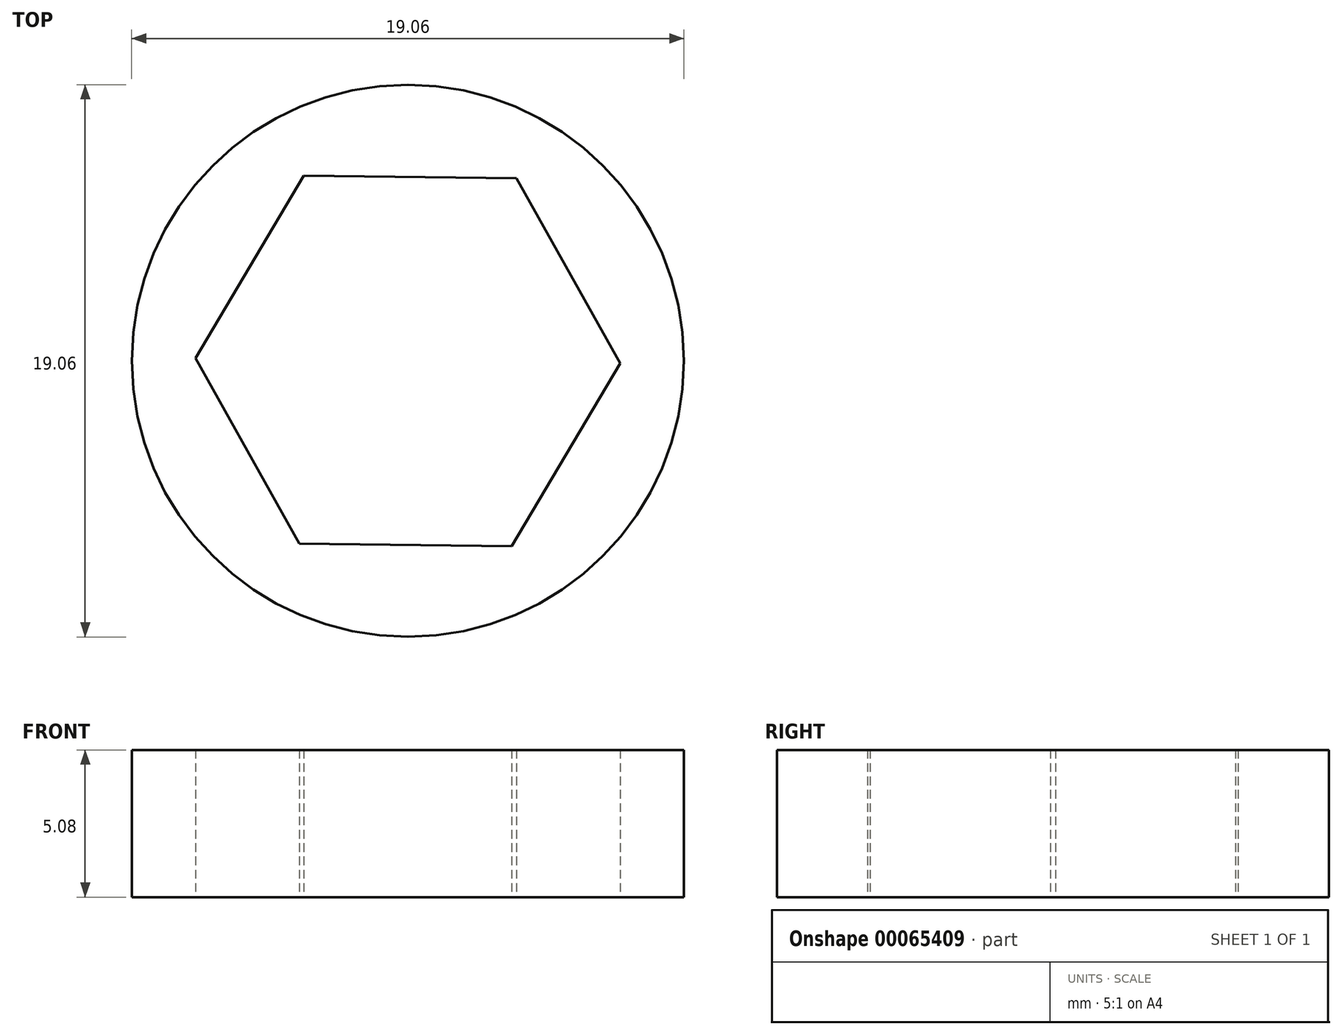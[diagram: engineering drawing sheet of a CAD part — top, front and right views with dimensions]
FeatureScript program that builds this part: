
annotation { "Feature Type Name" : "Feature", "Feature Type Description" : "" }
export const myFeature = defineFeature(function(context is Context, id is Id, definition is map)
    precondition{}
    {
        {
            var Q0;
            Q0=qCreatedBy(makeId("Top.planeOp"),FACE);
            var sketch = newSketch(context, id + "F0", { "sketchPlane" : qUnion([Q0])});
            skCircle(sketch, "E0.cCircle", {"center": v(0, 0) * mm, "radius": 7.33 * mm, "construction": true});
            skLineSegment(sketch, "E0.0", {"start": v(3.74, 6.3) * mm, "end": v(7.33, -0.09) * mm});
            skLineSegment(sketch, "E0.1", {"start": v(7.33, -0.09) * mm, "end": v(3.59, -6.4) * mm});
            skLineSegment(sketch, "E0.2", {"start": v(3.59, -6.4) * mm, "end": v(-3.74, -6.3) * mm});
            skLineSegment(sketch, "E0.3", {"start": v(-3.74, -6.3) * mm, "end": v(-7.33, 0.09) * mm});
            skLineSegment(sketch, "E0.4", {"start": v(-7.33, 0.09) * mm, "end": v(-3.59, 6.4) * mm});
            skLineSegment(sketch, "E0.5", {"start": v(-3.59, 6.4) * mm, "end": v(3.74, 6.3) * mm});
            skCircle(sketch, "E1", {"center": v(0, 0) * mm, "radius": 9.53 * mm});
            skSolve(sketch);
        }
        {
            var Q0;
            Q0=makeQuery(id+"F0.imprint","IMPRINT",FACE,{"disambiguationData":[TD([[makeQuery(id+"F0.imprint","IMPRINT",EDGE,{"derivedFrom":sQuery(id+"F0.wireOp",EDGE,"E0.0")}),1.0]])]});
            extrude(context, id + "F1", {"entities" : qUnion([Q0]), "depth" : 5.08 * mm});
        }
    });
